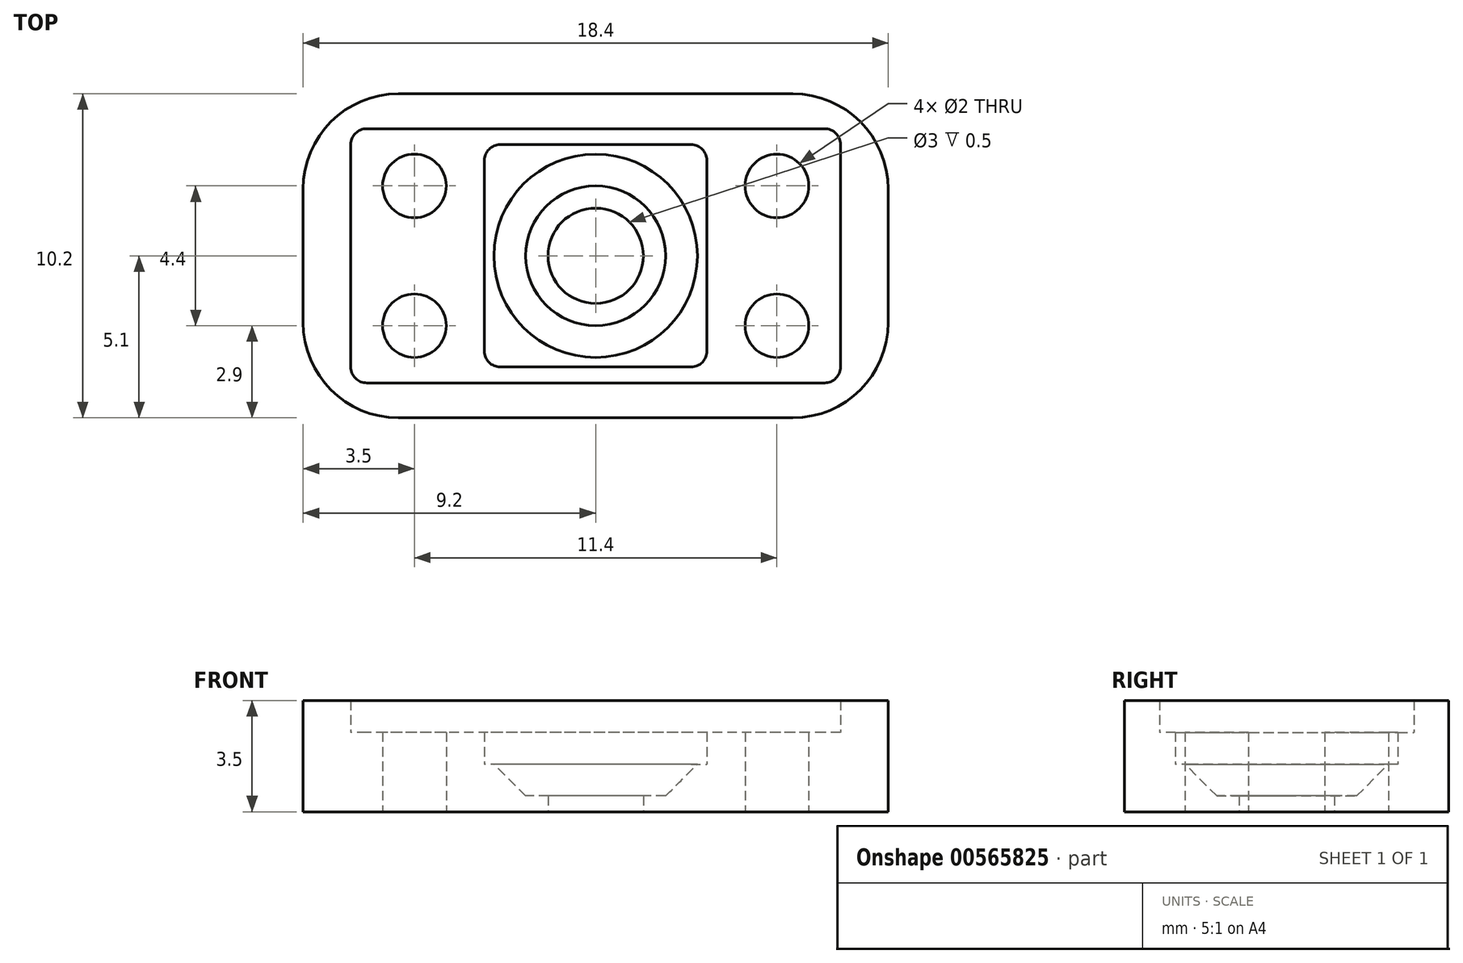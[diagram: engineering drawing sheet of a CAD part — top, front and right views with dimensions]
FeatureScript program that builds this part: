
annotation { "Feature Type Name" : "Feature", "Feature Type Description" : "" }
export const myFeature = defineFeature(function(context is Context, id is Id, definition is map)
    precondition{}
    {
        {
            var Q0;
            Q0=qCreatedBy(makeId("Top.planeOp"),FACE);
            var sketch = newSketch(context, id + "F0", { "sketchPlane" : qUnion([Q0])});
            skLineSegment(sketch, "E0.bottom", {"start": v(6.2, -5.1) * mm, "end": v(-6.2, -5.1) * mm});
            skLineSegment(sketch, "E0.top", {"start": v(6.2, 5.1) * mm, "end": v(-6.2, 5.1) * mm});
            skLineSegment(sketch, "E0.left", {"start": v(9.2, -2.1) * mm, "end": v(9.2, 2.1) * mm});
            skLineSegment(sketch, "E0.right", {"start": v(-9.2, -2.1) * mm, "end": v(-9.2, 2.1) * mm});
            skPoint(sketch, "E0.middle", {"position": v(0, 0) * mm});
            skPoint(sketch, "E1.visualSharp", {"position": v(-9.2, 5.1) * mm});
            skArc(sketch, "E1.filletArc", {"start": v(-6.2, 5.1) * mm, "mid": v(-8.32, 4.22) * mm, "end": v(-9.2, 2.1) * mm});
            skPoint(sketch, "E2.visualSharp", {"position": v(9.2, 5.1) * mm});
            skArc(sketch, "E2.filletArc", {"start": v(9.2, 2.1) * mm, "mid": v(8.32, 4.22) * mm, "end": v(6.2, 5.1) * mm});
            skPoint(sketch, "E3.visualSharp", {"position": v(-9.2, -5.1) * mm});
            skArc(sketch, "E3.filletArc", {"start": v(-9.2, -2.1) * mm, "mid": v(-8.32, -4.22) * mm, "end": v(-6.2, -5.1) * mm});
            skPoint(sketch, "E4.visualSharp", {"position": v(9.2, -5.1) * mm});
            skArc(sketch, "E4.filletArc", {"start": v(6.2, -5.1) * mm, "mid": v(8.32, -4.22) * mm, "end": v(9.2, -2.1) * mm});
            skCircle(sketch, "E5", {"center": v(0, 0) * mm, "radius": 1.5 * mm});
            skCircle(sketch, "E6", {"center": v(-5.7, 2.2) * mm, "radius": 1 * mm});
            skCircle(sketch, "E7.0.1.0", {"center": v(-5.7, -2.2) * mm, "radius": 1 * mm});
            skCircle(sketch, "E7.1.0.0", {"center": v(5.7, 2.2) * mm, "radius": 1 * mm});
            skCircle(sketch, "E7.1.1.0", {"center": v(5.7, -2.2) * mm, "radius": 1 * mm});
            skLineSegment(sketch, "E7.direction1", {"start": v(-5.7, 2.2) * mm, "end": v(5.7, 2.2) * mm, "construction": true});
            skLineSegment(sketch, "E7.direction2", {"start": v(-5.7, 2.2) * mm, "end": v(-5.7, -2.2) * mm, "construction": true});
            skSolve(sketch);
        }
        {
            var Q0;
            Q0=makeQuery(id+"F0.imprint","IMPRINT",FACE,{"disambiguationData":[TD([[makeQuery(id+"F0.imprint","IMPRINT",EDGE,{"derivedFrom":sQuery(id+"F0.wireOp",EDGE,"E0.bottom")}),-1.0]])]});
            extrude(context, id + "F1", {"entities" : qUnion([Q0]), "depth" : 0.5 * mm, "offsetDistance" : 25 * mm});
        }
        {
            var Q0;
            Q0=makeQuery(id+"F1.opExtrude","CAP_FACE",FACE,{"disambiguationData":[OSD([sQuery(id+"F0.wireOp",EDGE,"E0.bottom"),sQuery(id+"F0.wireOp",EDGE,"E0.top"),sQuery(id+"F0.wireOp",EDGE,"E0.left"),sQuery(id+"F0.wireOp",EDGE,"E0.right"),sQuery(id+"F0.wireOp",EDGE,"E1.filletArc"),sQuery(id+"F0.wireOp",EDGE,"E2.filletArc"),sQuery(id+"F0.wireOp",EDGE,"E3.filletArc"),sQuery(id+"F0.wireOp",EDGE,"E4.filletArc"),sQuery(id+"F0.wireOp",EDGE,"E5"),sQuery(id+"F0.wireOp",EDGE,"E6"),sQuery(id+"F0.wireOp",EDGE,"E7.0.1.0"),sQuery(id+"F0.wireOp",EDGE,"E7.1.0.0"),sQuery(id+"F0.wireOp",EDGE,"E7.1.1.0")])],"isStart":false});
            var sketch = newSketch(context, id + "F2", { "sketchPlane" : qUnion([Q0])});
            skPoint(sketch, "E8.middle", {"position": v(0, 0) * mm});
            skCircle(sketch, "E9", {"center": v(0, 0) * mm, "radius": 2.2 * mm});
            skSolve(sketch);
        }
        {
            var Q0;
            Q0=makeQuery(id+"F2.imprint","IMPRINT",FACE,{"disambiguationData":[TD([[makeQuery(id+"F2.imprint","IMPRINT",EDGE,{"derivedFrom":sQuery(id+"F2.wireOp",EDGE,"E9")}),-1.0]])]});
            extrude(context, id + "F3", {"entities" : qUnion([Q0]), "operationType" : NewBodyOperationType.ADD, "depth" : 1 * mm, "offsetDistance" : 25 * mm});
        }
        {
            var Q0;
            Q0=makeQuery(id+"F3.opExtrude","CAP_EDGE",EDGE,{"disambiguationData":[OSD([sQuery(id+"F2.wireOp",EDGE,"E9")])],"isStart":false});
            chamfer(context, id + "F4", {"entities" : qUnion([Q0]), "width" : 1 * mm, "tangentPropagation" : true});
        }
        {
            var Q0;
            Q0=makeQuery(id+"F3.opExtrude","CAP_FACE",FACE,{"disambiguationData":[OSD([sQuery(id+"F0.wireOp",EDGE,"E0.bottom"),sQuery(id+"F0.wireOp",EDGE,"E0.top"),sQuery(id+"F0.wireOp",EDGE,"E0.left"),sQuery(id+"F0.wireOp",EDGE,"E0.right"),sQuery(id+"F0.wireOp",EDGE,"E1.filletArc"),sQuery(id+"F0.wireOp",EDGE,"E2.filletArc"),sQuery(id+"F0.wireOp",EDGE,"E3.filletArc"),sQuery(id+"F0.wireOp",EDGE,"E4.filletArc"),sQuery(id+"F0.wireOp",EDGE,"E6"),sQuery(id+"F0.wireOp",EDGE,"E7.0.1.0"),sQuery(id+"F0.wireOp",EDGE,"E7.1.0.0"),sQuery(id+"F0.wireOp",EDGE,"E7.1.1.0"),sQuery(id+"F2.wireOp",EDGE,"E9")])],"isStart":false});
            var sketch = newSketch(context, id + "F5", { "sketchPlane" : qUnion([Q0])});
            skLineSegment(sketch, "E10.bottom", {"start": v(3, -3.5) * mm, "end": v(-3, -3.5) * mm});
            skLineSegment(sketch, "E10.top", {"start": v(3, 3.5) * mm, "end": v(-3, 3.5) * mm});
            skLineSegment(sketch, "E10.left", {"start": v(3.5, -3) * mm, "end": v(3.5, 3) * mm});
            skLineSegment(sketch, "E10.right", {"start": v(-3.5, -3) * mm, "end": v(-3.5, 3) * mm});
            skPoint(sketch, "E10.middle", {"position": v(0, 0) * mm});
            skPoint(sketch, "E11.visualSharp", {"position": v(-3.5, 3.5) * mm});
            skArc(sketch, "E11.filletArc", {"start": v(-3, 3.5) * mm, "mid": v(-3.35, 3.35) * mm, "end": v(-3.5, 3) * mm});
            skPoint(sketch, "E12.visualSharp", {"position": v(3.5, 3.5) * mm});
            skArc(sketch, "E12.filletArc", {"start": v(3.5, 3) * mm, "mid": v(3.35, 3.35) * mm, "end": v(3, 3.5) * mm});
            skPoint(sketch, "E13.visualSharp", {"position": v(-3.5, -3.5) * mm});
            skArc(sketch, "E13.filletArc", {"start": v(-3.5, -3) * mm, "mid": v(-3.35, -3.35) * mm, "end": v(-3, -3.5) * mm});
            skPoint(sketch, "E14.visualSharp", {"position": v(3.5, -3.5) * mm});
            skArc(sketch, "E14.filletArc", {"start": v(3, -3.5) * mm, "mid": v(3.35, -3.35) * mm, "end": v(3.5, -3) * mm});
            skSolve(sketch);
        }
        {
            var Q0;
            Q0=makeQuery(id+"F5.imprint","IMPRINT",FACE,{"disambiguationData":[TD([[makeQuery(id+"F5.imprint","IMPRINT",EDGE,{"derivedFrom":sQuery(id+"F5.wireOp",EDGE,"E10.bottom")}),1.0]])]});
            extrude(context, id + "F6", {"entities" : qUnion([Q0]), "operationType" : NewBodyOperationType.ADD, "depth" : 1 * mm, "offsetDistance" : 25 * mm});
        }
        {
            var Q0;
            Q0=makeQuery(id+"F6.opExtrude","CAP_FACE",FACE,{"disambiguationData":[OSD([sQuery(id+"F0.wireOp",EDGE,"E0.bottom"),sQuery(id+"F0.wireOp",EDGE,"E0.top"),sQuery(id+"F0.wireOp",EDGE,"E0.left"),sQuery(id+"F0.wireOp",EDGE,"E0.right"),sQuery(id+"F0.wireOp",EDGE,"E1.filletArc"),sQuery(id+"F0.wireOp",EDGE,"E2.filletArc"),sQuery(id+"F0.wireOp",EDGE,"E3.filletArc"),sQuery(id+"F0.wireOp",EDGE,"E4.filletArc"),sQuery(id+"F0.wireOp",EDGE,"E6"),sQuery(id+"F0.wireOp",EDGE,"E7.0.1.0"),sQuery(id+"F0.wireOp",EDGE,"E7.1.0.0"),sQuery(id+"F0.wireOp",EDGE,"E7.1.1.0"),sQuery(id+"F5.wireOp",EDGE,"E10.bottom"),sQuery(id+"F5.wireOp",EDGE,"E10.top"),sQuery(id+"F5.wireOp",EDGE,"E10.left"),sQuery(id+"F5.wireOp",EDGE,"E10.right"),sQuery(id+"F5.wireOp",EDGE,"E11.filletArc"),sQuery(id+"F5.wireOp",EDGE,"E12.filletArc"),sQuery(id+"F5.wireOp",EDGE,"E13.filletArc"),sQuery(id+"F5.wireOp",EDGE,"E14.filletArc")])],"isStart":false});
            var sketch = newSketch(context, id + "F7", { "sketchPlane" : qUnion([Q0])});
            skLineSegment(sketch, "E15.bottom", {"start": v(7.2, -4) * mm, "end": v(-7.2, -4) * mm});
            skLineSegment(sketch, "E15.top", {"start": v(7.2, 4) * mm, "end": v(-7.2, 4) * mm});
            skLineSegment(sketch, "E15.left", {"start": v(7.7, -3.5) * mm, "end": v(7.7, 3.5) * mm});
            skLineSegment(sketch, "E15.right", {"start": v(-7.7, -3.5) * mm, "end": v(-7.7, 3.5) * mm});
            skPoint(sketch, "E15.middle", {"position": v(0, 0) * mm});
            skPoint(sketch, "E16.visualSharp", {"position": v(-7.7, 4) * mm});
            skArc(sketch, "E16.filletArc", {"start": v(-7.2, 4) * mm, "mid": v(-7.55, 3.85) * mm, "end": v(-7.7, 3.5) * mm});
            skPoint(sketch, "E17.visualSharp", {"position": v(7.7, 4) * mm});
            skArc(sketch, "E17.filletArc", {"start": v(7.7, 3.5) * mm, "mid": v(7.55, 3.85) * mm, "end": v(7.2, 4) * mm});
            skPoint(sketch, "E18.visualSharp", {"position": v(7.7, -4) * mm});
            skArc(sketch, "E18.filletArc", {"start": v(7.2, -4) * mm, "mid": v(7.55, -3.85) * mm, "end": v(7.7, -3.5) * mm});
            skPoint(sketch, "E19.visualSharp", {"position": v(-7.7, -4) * mm});
            skArc(sketch, "E19.filletArc", {"start": v(-7.7, -3.5) * mm, "mid": v(-7.55, -3.85) * mm, "end": v(-7.2, -4) * mm});
            skSolve(sketch);
        }
        {
            var Q0;
            Q0=makeQuery(id+"F7.imprint","IMPRINT",FACE,{"disambiguationData":[TD([[makeQuery(id+"F7.imprint","IMPRINT",EDGE,{"derivedFrom":sQuery(id+"F7.wireOp",EDGE,"E15.bottom")}),1.0]])]});
            extrude(context, id + "F8", {"entities" : qUnion([Q0]), "operationType" : NewBodyOperationType.ADD, "depth" : 1 * mm, "offsetDistance" : 25 * mm});
        }
    });
